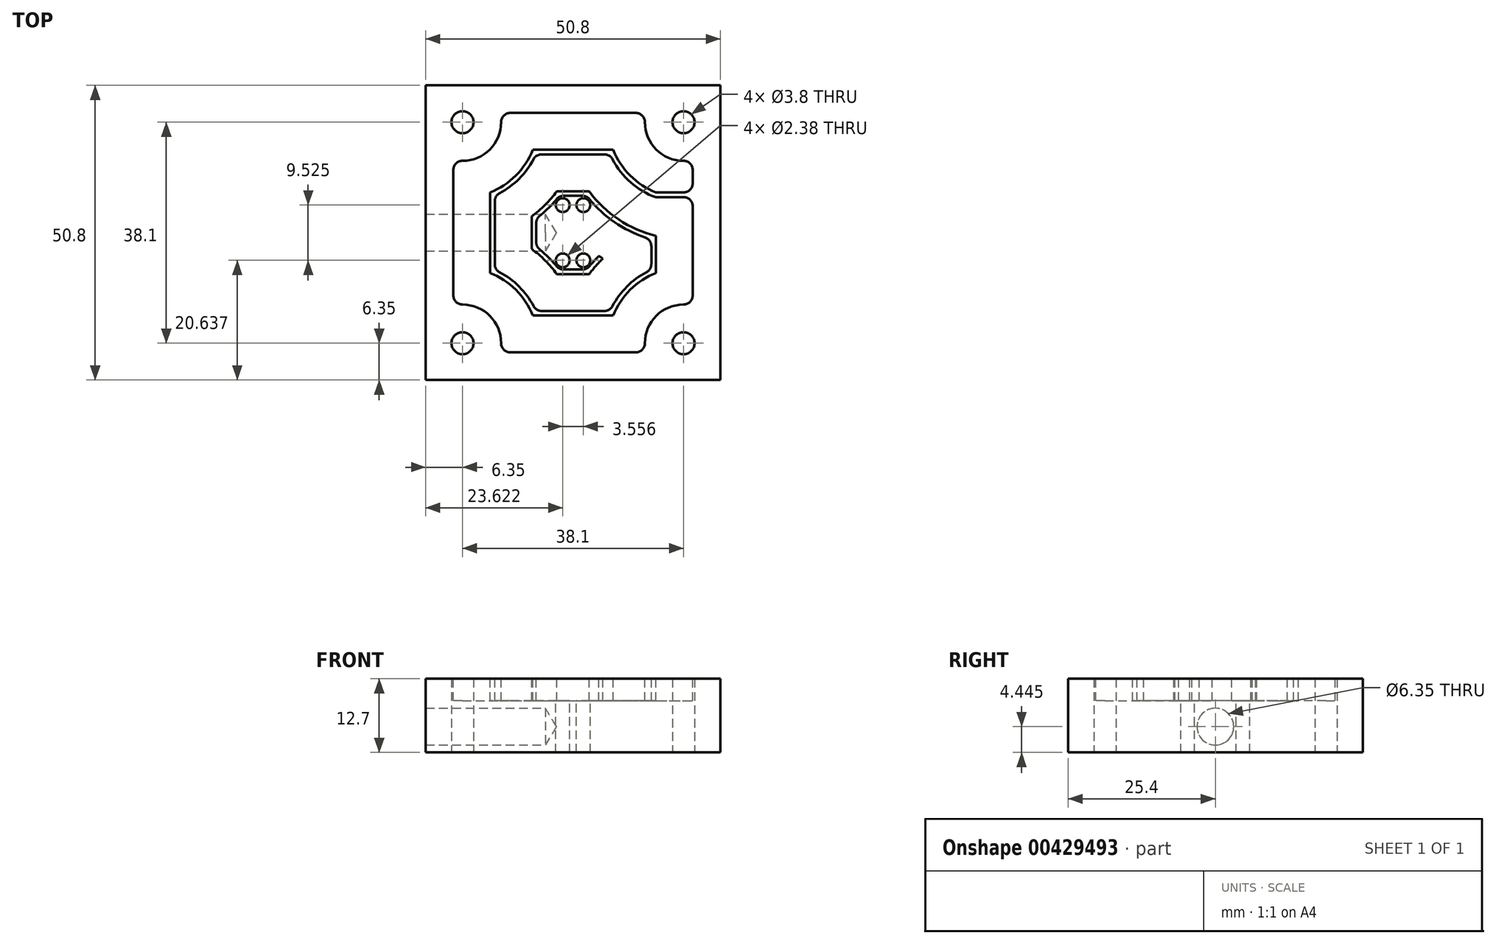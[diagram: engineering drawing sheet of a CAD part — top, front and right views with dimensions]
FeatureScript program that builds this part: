
annotation { "Feature Type Name" : "Feature", "Feature Type Description" : "" }
export const myFeature = defineFeature(function(context is Context, id is Id, definition is map)
    precondition{}
    {
        {
            var Q0;
            Q0=qCreatedBy(makeId("Top.planeOp"),FACE);
            var sketch = newSketch(context, id + "F0", { "sketchPlane" : qUnion([Q0])});
            skLineSegment(sketch, "E0.bottom", {"start": v(-25.4, 25.4) * mm, "end": v(25.4, 25.4) * mm});
            skLineSegment(sketch, "E0.top", {"start": v(-25.4, -25.4) * mm, "end": v(25.4, -25.4) * mm});
            skLineSegment(sketch, "E0.left", {"start": v(-25.4, 25.4) * mm, "end": v(-25.4, -25.4) * mm});
            skLineSegment(sketch, "E0.right", {"start": v(25.4, 25.4) * mm, "end": v(25.4, -25.4) * mm});
            skSolve(sketch);
        }
        {
            var Q0;
            Q0=makeQuery(id+"F0.imprint","IMPRINT",FACE,{"disambiguationData":[TD([[makeQuery(id+"F0.imprint","IMPRINT",EDGE,{"derivedFrom":sQuery(id+"F0.wireOp",EDGE,"E0.bottom")}),-1.0]])]});
            extrude(context, id + "F1", {"entities" : qUnion([Q0]), "depth" : 12.7 * mm, "offsetDistance" : 25.4 * mm});
        }
        {
            var Q0;
            Q0=makeQuery(id+"F1.opExtrude","CAP_FACE",FACE,{"disambiguationData":[OSD([sQuery(id+"F0.wireOp",EDGE,"E0.bottom"),sQuery(id+"F0.wireOp",EDGE,"E0.top"),sQuery(id+"F0.wireOp",EDGE,"E0.left"),sQuery(id+"F0.wireOp",EDGE,"E0.right")])],"isStart":false});
            var sketch = newSketch(context, id + "F2", { "sketchPlane" : qUnion([Q0])});
            skPoint(sketch, "E1", {"position": v(19.05, 19.05) * mm});
            skLineSegment(sketch, "E2", {"start": v(12.7, 25.4) * mm, "end": v(12.7, -22.23) * mm, "construction": true});
            skPoint(sketch, "E3.MirrorP", {"position": v(19.05, -19.05) * mm});
            skPoint(sketch, "E4.MirrorP", {"position": v(-19.05, -19.05) * mm});
            skPoint(sketch, "E5.MirrorP", {"position": v(-19.05, 19.05) * mm});
            skLineSegment(sketch, "E6.0", {"start": v(14.29, 25.4) * mm, "end": v(14.29, -3.17) * mm, "construction": true});
            skLineSegment(sketch, "E7.MirrorCS", {"start": v(11.11, 25.4) * mm, "end": v(11.11, -3.17) * mm, "construction": true});
            skCircle(sketch, "E8", {"center": v(19.05, 19.05) * mm, "radius": 1.75 * mm, "construction": true});
            skCircle(sketch, "E9.MirrorC", {"center": v(19.05, -19.05) * mm, "radius": 1.75 * mm, "construction": true});
            skCircle(sketch, "E10.MirrorC", {"center": v(-19.05, 19.05) * mm, "radius": 1.75 * mm, "construction": true});
            skCircle(sketch, "E11.MirrorC", {"center": v(-19.05, -19.05) * mm, "radius": 1.75 * mm, "construction": true});
            skLineSegment(sketch, "E12", {"start": v(-25.4, 0) * mm, "end": v(25.4, 0) * mm, "construction": true});
            skLineSegment(sketch, "E13.0", {"start": v(-25.4, -3.18) * mm, "end": v(25.4, -3.17) * mm, "construction": true});
            skLineSegment(sketch, "E14.MirrorCS", {"start": v(-25.4, 3.18) * mm, "end": v(25.4, 3.17) * mm, "construction": true});
            skCircle(sketch, "E15", {"center": v(0, 0) * mm, "radius": 22.23 * mm, "construction": true});
            skLineSegment(sketch, "E16.0", {"start": v(-22.23, -4.76) * mm, "end": v(22.23, -4.76) * mm});
            skLineSegment(sketch, "E17.0", {"start": v(-20.64, -6.35) * mm, "end": v(22.23, -6.35) * mm});
            skLineSegment(sketch, "E18.0", {"start": v(-20.76, -7.94) * mm, "end": v(22.23, -7.94) * mm});
            skLineSegment(sketch, "E19.0", {"start": v(-22.23, -9.53) * mm, "end": v(20.64, -9.52) * mm});
            skLineSegment(sketch, "E20.0", {"start": v(-22.23, -11.11) * mm, "end": v(20.64, -11.11) * mm});
            skLineSegment(sketch, "E21.0", {"start": v(-20.64, -12.7) * mm, "end": v(22.23, -12.7) * mm});
            skLineSegment(sketch, "E22.0", {"start": v(-20.64, -14.29) * mm, "end": v(13.5, -14.29) * mm});
            skLineSegment(sketch, "E23.0", {"start": v(-22.23, -15.88) * mm, "end": v(13.5, -15.88) * mm});
            skLineSegment(sketch, "E24.0", {"start": v(-25.4, -22.23) * mm, "end": v(25.4, -22.22) * mm});
            skLineSegment(sketch, "E25.0", {"start": v(-25.4, 25.4) * mm, "end": v(-25.4, -25.4) * mm, "construction": true});
            skLineSegment(sketch, "E26.trimOffspring", {"start": v(-20.64, -12.7) * mm, "end": v(-20.64, -14.29) * mm, "construction": true});
            skLineSegment(sketch, "E27.trimOffspring", {"start": v(20.64, -9.52) * mm, "end": v(20.64, -11.11) * mm});
            skLineSegment(sketch, "E28.trimOffspring", {"start": v(22.23, -7.94) * mm, "end": v(22.23, -12.7) * mm});
            skLineSegment(sketch, "E29.trimOffspring", {"start": v(-20.64, -6.35) * mm, "end": v(-20.64, -7.94) * mm, "construction": true});
            skLineSegment(sketch, "E30.trimOffspring", {"start": v(22.23, -4.76) * mm, "end": v(22.23, -6.35) * mm});
            skLineSegment(sketch, "E31.trimOffspring", {"start": v(-22.23, -4.76) * mm, "end": v(-22.23, -9.53) * mm, "construction": true});
            skLineSegment(sketch, "E32.trimOffspring", {"start": v(-22.23, -11.11) * mm, "end": v(-22.23, -15.88) * mm, "construction": true});
            skLineSegment(sketch, "E33.trimOffspring", {"start": v(11.9, -14.29) * mm, "end": v(11.9, -15.88) * mm});
            skLineSegment(sketch, "E34.trimOffspring", {"start": v(13.5, -14.29) * mm, "end": v(13.5, -15.88) * mm});
            skSolve(sketch);
        }
        {
            var Q0;
            {var subQ1=sQuery(id+"F2.wireOp",EDGE,"E24.0");Q0=makeQuery(id+"F2.imprint","IMPRINT",FACE,{"disambiguationData":[TD([[makeQuery(id+"F2.imprint","IMPRINT",EDGE,{"derivedFrom":subQ1}),1.0]])]});}
            var sketch = newSketch(context, id + "F3", { "sketchPlane" : qUnion([Q0])});
            skLineSegment(sketch, "E35.0", {"start": v(-25.4, 3.18) * mm, "end": v(25.4, 3.17) * mm, "construction": true});
            skLineSegment(sketch, "E36.0", {"start": v(-25.4, -3.18) * mm, "end": v(25.4, -3.17) * mm, "construction": true});
            skLineSegment(sketch, "E37.0", {"start": v(12.7, 25.4) * mm, "end": v(12.7, -22.23) * mm, "construction": true});
            skLineSegment(sketch, "E38.0", {"start": v(14.29, 25.4) * mm, "end": v(14.29, -3.17) * mm, "construction": true});
            skCircle(sketch, "E39.0", {"center": v(19.05, -19.05) * mm, "radius": 1.75 * mm, "construction": true});
            skCircle(sketch, "E40.0", {"center": v(19.05, 19.05) * mm, "radius": 1.75 * mm, "construction": true});
            skCircle(sketch, "E41.0", {"center": v(-19.05, 19.05) * mm, "radius": 1.75 * mm, "construction": true});
            skCircle(sketch, "E42.0", {"center": v(-19.05, -19.05) * mm, "radius": 1.75 * mm, "construction": true});
            skLineSegment(sketch, "E43.0", {"start": v(-25.4, -25.4) * mm, "end": v(25.4, -25.4) * mm, "construction": true});
            skLineSegment(sketch, "E44.0", {"start": v(25.4, 25.4) * mm, "end": v(25.4, -25.4) * mm, "construction": true});
            skLineSegment(sketch, "E45.0", {"start": v(-25.4, 25.4) * mm, "end": v(25.4, 25.4) * mm, "construction": true});
            skLineSegment(sketch, "E46.0", {"start": v(-25.4, 25.4) * mm, "end": v(-25.4, -25.4) * mm, "construction": true});
            skArc(sketch, "E47.0", {"start": v(14.29, 20.31) * mm, "mid": v(15.14, 16.05) * mm, "end": v(19.05, 14.12) * mm});
            skArc(sketch, "E48.0", {"start": v(-14.12, -19.05) * mm, "mid": v(-15.57, -15.57) * mm, "end": v(-19.05, -14.12) * mm});
            skArc(sketch, "E49.MirrorC", {"start": v(14.12, -19.05) * mm, "mid": v(15.57, -15.57) * mm, "end": v(19.05, -14.12) * mm});
            skArc(sketch, "E50.MirrorC", {"start": v(-14.12, 19.05) * mm, "mid": v(-15.57, 15.57) * mm, "end": v(-19.05, 14.12) * mm});
            skArc(sketch, "E51.trimOffspring", {"start": v(9.36, -19.05) * mm, "mid": v(11.66, -12.78) * mm, "end": v(17.46, -9.5) * mm});
            skArc(sketch, "E52.MirrorCS", {"start": v(9.5, 17.46) * mm, "mid": v(12.2, 12.2) * mm, "end": v(17.46, 9.5) * mm});
            skLineSegment(sketch, "E53", {"start": v(9.36, -19.05) * mm, "end": v(9.36, -22.23) * mm});
            skArc(sketch, "E54.MirrorCS", {"start": v(-9.5, 17.46) * mm, "mid": v(-12.2, 12.2) * mm, "end": v(-17.46, 9.5) * mm});
            skArc(sketch, "E55.MirrorCS", {"start": v(-9.5, -17.46) * mm, "mid": v(-12.2, -12.2) * mm, "end": v(-17.46, -9.5) * mm});
            skPoint(sketch, "E56.orphan", {"position": v(-9.36, -19.05) * mm});
            skLineSegment(sketch, "E57.trimOffspring", {"start": v(-9.5, 17.46) * mm, "end": v(9.5, 17.46) * mm});
            skLineSegment(sketch, "E58.trimOffspring", {"start": v(-9.5, -17.46) * mm, "end": v(3.89, -17.46) * mm});
            skLineSegment(sketch, "E59", {"start": v(19.05, -14.12) * mm, "end": v(19.84, -14.12) * mm});
            skLineSegment(sketch, "E60.MirrorCS", {"start": v(19.05, 14.12) * mm, "end": v(19.84, 14.12) * mm});
            skLineSegment(sketch, "E61.MirrorCS", {"start": v(-19.05, 14.12) * mm, "end": v(-19.84, 14.12) * mm});
            skLineSegment(sketch, "E62.MirrorCS", {"start": v(-19.05, -14.12) * mm, "end": v(-19.84, -14.12) * mm});
            skLineSegment(sketch, "E63", {"start": v(14.12, -19.05) * mm, "end": v(14.12, -34.5) * mm});
            skLineSegment(sketch, "E64.MirrorCS", {"start": v(14.12, 19.05) * mm, "end": v(14.12, 19.84) * mm});
            skLineSegment(sketch, "E65.MirrorCS", {"start": v(-14.12, 19.05) * mm, "end": v(-14.12, 19.84) * mm});
            skLineSegment(sketch, "E66.MirrorCS", {"start": v(-14.12, -19.05) * mm, "end": v(-14.12, -19.84) * mm});
            skLineSegment(sketch, "E67.trimOffspring", {"start": v(-17.46, 9.5) * mm, "end": v(-17.46, -9.5) * mm});
            skLineSegment(sketch, "E68.trimOffspring", {"start": v(17.46, 9.5) * mm, "end": v(17.46, -9.5) * mm});
            skLineSegment(sketch, "E69.trimOffspring", {"start": v(22.23, 11.74) * mm, "end": v(22.23, -11.74) * mm});
            skLineSegment(sketch, "E70.trimOffspring", {"start": v(-11.74, 22.23) * mm, "end": v(11.74, 22.23) * mm});
            skLineSegment(sketch, "E71.trimOffspring", {"start": v(-11.74, -22.23) * mm, "end": v(6.18, -22.23) * mm});
            skLineSegment(sketch, "E72.trimOffspring", {"start": v(-22.23, 11.74) * mm, "end": v(-22.23, -11.74) * mm});
            skPoint(sketch, "E73.visualSharp", {"position": v(22.23, -14.12) * mm});
            skArc(sketch, "E73.filletArc", {"start": v(19.84, -14.12) * mm, "mid": v(21.53, -13.42) * mm, "end": v(22.23, -11.74) * mm});
            skPoint(sketch, "E74.visualSharp", {"position": v(22.23, 14.12) * mm});
            skArc(sketch, "E74.filletArc", {"start": v(22.23, 11.74) * mm, "mid": v(21.53, 13.42) * mm, "end": v(19.84, 14.12) * mm});
            skPoint(sketch, "E75.visualSharp", {"position": v(14.12, 22.23) * mm});
            skArc(sketch, "E75.filletArc", {"start": v(14.12, 19.84) * mm, "mid": v(13.42, 21.53) * mm, "end": v(11.74, 22.23) * mm});
            skPoint(sketch, "E76.visualSharp", {"position": v(-14.12, 22.23) * mm});
            skArc(sketch, "E76.filletArc", {"start": v(-11.74, 22.23) * mm, "mid": v(-13.42, 21.53) * mm, "end": v(-14.12, 19.84) * mm});
            skPoint(sketch, "E77.visualSharp", {"position": v(-22.23, 14.12) * mm});
            skArc(sketch, "E77.filletArc", {"start": v(-19.84, 14.12) * mm, "mid": v(-21.53, 13.42) * mm, "end": v(-22.23, 11.74) * mm});
            skPoint(sketch, "E78.visualSharp", {"position": v(-22.23, -14.12) * mm});
            skArc(sketch, "E78.filletArc", {"start": v(-22.23, -11.74) * mm, "mid": v(-21.53, -13.42) * mm, "end": v(-19.84, -14.12) * mm});
            skPoint(sketch, "E79.visualSharp", {"position": v(-14.12, -22.23) * mm});
            skArc(sketch, "E79.filletArc", {"start": v(-14.12, -19.84) * mm, "mid": v(-13.42, -21.53) * mm, "end": v(-11.74, -22.23) * mm});
            skLineSegment(sketch, "E80.0", {"start": v(8.57, -19.05) * mm, "end": v(8.57, -19.84) * mm});
            skArc(sketch, "E81.0", {"start": v(8.57, -19.05) * mm, "mid": v(10.37, -13.17) * mm, "end": v(15.17, -9.31) * mm});
            skLineSegment(sketch, "E82.0", {"start": v(16.67, 7.1) * mm, "end": v(16.67, -7.1) * mm});
            skArc(sketch, "E83.0", {"start": v(9.31, 15.17) * mm, "mid": v(11.64, 11.64) * mm, "end": v(15.17, 9.31) * mm});
            skLineSegment(sketch, "E84.0", {"start": v(-7.1, 16.67) * mm, "end": v(7.1, 16.67) * mm});
            skArc(sketch, "E85.0", {"start": v(-9.31, 15.17) * mm, "mid": v(-11.64, 11.64) * mm, "end": v(-15.17, 9.31) * mm});
            skLineSegment(sketch, "E86.0", {"start": v(-16.67, 7.1) * mm, "end": v(-16.67, -7.1) * mm});
            skArc(sketch, "E87.0", {"start": v(-9.31, -15.17) * mm, "mid": v(-11.64, -11.64) * mm, "end": v(-15.17, -9.31) * mm});
            skLineSegment(sketch, "E88.0", {"start": v(-7.1, -16.67) * mm, "end": v(1.25, -16.67) * mm});
            skLineSegment(sketch, "E89.trimOffspring", {"start": v(9.36, -22.23) * mm, "end": v(14.12, -22.23) * mm});
            skPoint(sketch, "E90.visualSharp", {"position": v(8.57, -22.23) * mm});
            skArc(sketch, "E90.filletArc", {"start": v(6.18, -22.23) * mm, "mid": v(7.87, -21.53) * mm, "end": v(8.57, -19.84) * mm});
            skArc(sketch, "E91.0", {"start": v(3.89, -17.46) * mm, "mid": v(6.41, -10.52) * mm, "end": v(11.9, -5.58) * mm});
            skLineSegment(sketch, "E92.0", {"start": v(11.9, 5.58) * mm, "end": v(11.9, -5.58) * mm});
            skLineSegment(sketch, "E93.MirrorCS", {"start": v(-11.9, 5.58) * mm, "end": v(-11.9, -5.58) * mm});
            skLineSegment(sketch, "E94.0", {"start": v(-5.58, -11.9) * mm, "end": v(-0.49, -11.9) * mm});
            skLineSegment(sketch, "E95.0", {"start": v(-5.58, 11.9) * mm, "end": v(5.58, 11.9) * mm});
            skArc(sketch, "E96.trimOffspring", {"start": v(5.58, 11.9) * mm, "mid": v(8.27, 8.27) * mm, "end": v(11.9, 5.58) * mm});
            skArc(sketch, "E97.trimOffspring", {"start": v(-5.58, 11.9) * mm, "mid": v(-8.27, 8.27) * mm, "end": v(-11.9, 5.58) * mm});
            skArc(sketch, "E98.trimOffspring", {"start": v(-5.58, -11.9) * mm, "mid": v(-8.27, -8.27) * mm, "end": v(-11.9, -5.58) * mm});
            skPoint(sketch, "E99.visualSharp", {"position": v(16.67, -8.84) * mm});
            skArc(sketch, "E99.filletArc", {"start": v(15.17, -9.31) * mm, "mid": v(16.26, -8.44) * mm, "end": v(16.67, -7.1) * mm});
            skPoint(sketch, "E100.visualSharp", {"position": v(16.67, 8.84) * mm});
            skArc(sketch, "E100.filletArc", {"start": v(16.67, 7.1) * mm, "mid": v(16.26, 8.44) * mm, "end": v(15.17, 9.31) * mm});
            skPoint(sketch, "E101.visualSharp", {"position": v(8.84, 16.67) * mm});
            skArc(sketch, "E101.filletArc", {"start": v(9.31, 15.17) * mm, "mid": v(8.44, 16.26) * mm, "end": v(7.1, 16.67) * mm});
            skPoint(sketch, "E102.visualSharp", {"position": v(-8.84, 16.67) * mm});
            skArc(sketch, "E102.filletArc", {"start": v(-7.1, 16.67) * mm, "mid": v(-8.44, 16.26) * mm, "end": v(-9.31, 15.17) * mm});
            skPoint(sketch, "E103.visualSharp", {"position": v(-16.67, 8.84) * mm});
            skArc(sketch, "E103.filletArc", {"start": v(-15.17, 9.31) * mm, "mid": v(-16.26, 8.44) * mm, "end": v(-16.67, 7.1) * mm});
            skPoint(sketch, "E104.visualSharp", {"position": v(-16.67, -8.84) * mm});
            skArc(sketch, "E104.filletArc", {"start": v(-16.67, -7.1) * mm, "mid": v(-16.26, -8.44) * mm, "end": v(-15.17, -9.31) * mm});
            skPoint(sketch, "E105.visualSharp", {"position": v(-8.84, -16.67) * mm});
            skArc(sketch, "E105.filletArc", {"start": v(-9.31, -15.17) * mm, "mid": v(-8.44, -16.26) * mm, "end": v(-7.1, -16.67) * mm});
            skArc(sketch, "E106.0", {"start": v(3.56, -14.9) * mm, "mid": v(5.98, -9.74) * mm, "end": v(10.07, -5.76) * mm});
            skLineSegment(sketch, "E107.0", {"start": v(11.11, 3.79) * mm, "end": v(11.11, -3.79) * mm});
            skArc(sketch, "E108.0", {"start": v(5.76, 10.07) * mm, "mid": v(7.7, 7.7) * mm, "end": v(10.07, 5.76) * mm});
            skLineSegment(sketch, "E109.0", {"start": v(-3.79, 11.11) * mm, "end": v(3.79, 11.11) * mm});
            skArc(sketch, "E110.0", {"start": v(-5.76, 10.07) * mm, "mid": v(-7.7, 7.7) * mm, "end": v(-10.07, 5.76) * mm});
            skLineSegment(sketch, "E111.0", {"start": v(-11.11, 3.79) * mm, "end": v(-11.11, -3.79) * mm});
            skArc(sketch, "E112.0", {"start": v(-5.76, -10.07) * mm, "mid": v(-7.7, -7.7) * mm, "end": v(-10.07, -5.76) * mm});
            skArc(sketch, "E113.0", {"start": v(-0.49, -11.9) * mm, "mid": v(-0.34, -11.5) * mm, "end": v(-0.18, -11.11) * mm});
            skArc(sketch, "E114.0", {"start": v(2.57, 6.35) * mm, "mid": v(4.34, 4.34) * mm, "end": v(6.35, 2.57) * mm});
            skLineSegment(sketch, "E115.0", {"start": v(-2.57, 6.35) * mm, "end": v(2.57, 6.35) * mm});
            skArc(sketch, "E116.0", {"start": v(-2.57, 6.35) * mm, "mid": v(-4.34, 4.34) * mm, "end": v(-6.35, 2.57) * mm});
            skArc(sketch, "E117.0", {"start": v(-3.44, -5.3) * mm, "mid": v(-4.83, -3.87) * mm, "end": v(-6.35, -2.57) * mm});
            skArc(sketch, "E118.trimOffspring", {"start": v(-0.49, -11.9) * mm, "mid": v(2.27, -6.76) * mm, "end": v(6.35, -2.57) * mm});
            skLineSegment(sketch, "E119.trimOffspring", {"start": v(6.35, 2.57) * mm, "end": v(6.35, -2.57) * mm});
            skLineSegment(sketch, "E120.trimOffspring", {"start": v(-6.35, 2.57) * mm, "end": v(-6.35, -2.57) * mm});
            skPoint(sketch, "E121.visualSharp", {"position": v(11.11, -5.11) * mm});
            skArc(sketch, "E121.filletArc", {"start": v(10.07, -5.76) * mm, "mid": v(10.83, -4.9) * mm, "end": v(11.11, -3.79) * mm});
            skPoint(sketch, "E122.visualSharp", {"position": v(11.11, 5.11) * mm});
            skArc(sketch, "E122.filletArc", {"start": v(11.11, 3.79) * mm, "mid": v(10.83, 4.9) * mm, "end": v(10.07, 5.76) * mm});
            skPoint(sketch, "E123.visualSharp", {"position": v(5.11, 11.11) * mm});
            skArc(sketch, "E123.filletArc", {"start": v(5.76, 10.07) * mm, "mid": v(4.9, 10.83) * mm, "end": v(3.79, 11.11) * mm});
            skPoint(sketch, "E124.visualSharp", {"position": v(-5.11, 11.11) * mm});
            skArc(sketch, "E124.filletArc", {"start": v(-3.79, 11.11) * mm, "mid": v(-4.9, 10.83) * mm, "end": v(-5.76, 10.07) * mm});
            skPoint(sketch, "E125.visualSharp", {"position": v(-11.11, 5.11) * mm});
            skArc(sketch, "E125.filletArc", {"start": v(-10.07, 5.76) * mm, "mid": v(-10.83, 4.9) * mm, "end": v(-11.11, 3.79) * mm});
            skPoint(sketch, "E126.visualSharp", {"position": v(-11.11, -5.11) * mm});
            skArc(sketch, "E126.filletArc", {"start": v(-11.11, -3.79) * mm, "mid": v(-10.83, -4.9) * mm, "end": v(-10.07, -5.76) * mm});
            skArc(sketch, "E127.filletArc", {"start": v(-5.76, -10.07) * mm, "mid": v(-4.9, -10.83) * mm, "end": v(-3.79, -11.11) * mm});
            skPoint(sketch, "E128.visualSharp", {"position": v(3.19, -16.67) * mm});
            skArc(sketch, "E128.filletArc", {"start": v(1.25, -16.67) * mm, "mid": v(2.7, -16.18) * mm, "end": v(3.56, -14.9) * mm});
            skLineSegment(sketch, "E129.trimOffspring", {"start": v(-3.79, -11.11) * mm, "end": v(-2.6, -11.11) * mm});
            skArc(sketch, "E130.0", {"start": v(-0.44, -9.76) * mm, "mid": v(0.06, -8.76) * mm, "end": v(0.62, -7.8) * mm});
            skPoint(sketch, "E131.visualSharp", {"position": v(-1.03, -11.11) * mm});
            skArc(sketch, "E131.filletArc", {"start": v(-2.6, -11.11) * mm, "mid": v(-1.32, -10.75) * mm, "end": v(-0.44, -9.76) * mm});
            skPoint(sketch, "E132", {"position": v(0, -6.35) * mm});
            skArc(sketch, "E133", {"start": v(0.62, -7.8) * mm, "mid": v(-0.17, -4.53) * mm, "end": v(-3.44, -5.3) * mm});
            skLineSegment(sketch, "E134.extension", {"start": v(-3.44, -5.3) * mm, "end": v(-3.44, -5.3) * mm});
            skSolve(sketch);
        }
        {
            var Q0;
            Q0=makeQuery(id+"F1.opExtrude","SWEPT_FACE",FACE,{"disambiguationData":[OSD([sQuery(id+"F0.wireOp",EDGE,"E0.left")])]});
            var sketch = newSketch(context, id + "F4", { "sketchPlane" : qUnion([Q0])});
            skLineSegment(sketch, "E135.0", {"start": v(-25.4, 0) * mm, "end": v(25.4, 0) * mm, "construction": true});
            skLineSegment(sketch, "E136.0", {"start": v(-25.4, 4.45) * mm, "end": v(25.4, 4.45) * mm, "construction": true});
            skPoint(sketch, "E137", {"position": v(0, 4.45) * mm});
            skLineSegment(sketch, "E138.0", {"start": v(-25.4, 12.7) * mm, "end": v(-25.4, 0) * mm, "construction": true});
            skLineSegment(sketch, "E139.0", {"start": v(25.4, 12.7) * mm, "end": v(25.4, 0) * mm, "construction": true});
            skSolve(sketch);
        }
        {
            var Q0;
            Q0=sQuery(id+"F4.wireOp",VERTEX,"E137");
            var Q1;
            Q1=makeQuery(id+"F1.opExtrude","SWEPT_BODY",BODY,{"disambiguationData":[OSD([sQuery(id+"F0.wireOp",EDGE,"E0.bottom"),sQuery(id+"F0.wireOp",EDGE,"E0.top"),sQuery(id+"F0.wireOp",EDGE,"E0.left"),sQuery(id+"F0.wireOp",EDGE,"E0.right")])]});
            hole(context, id + "F5", {"style" : HoleStyle.SIMPLE, "endStyle" : HoleEndStyle.BLIND, "holeDiameter" : 6.35 * mm, "majorDiameter" : 6.35 * mm, "holeDepth" : 20.64 * mm, "isTappedThrough" : true, "tappedDepth" : 4.44 * mm, "tapClearance" : 3, "locations" : qUnion([Q0]), "scope" : qUnion([Q1]), "startStyle" : HoleStartStyle.PART});
        }
        {
            var Q0;
            Q0=makeQuery(id+"F1.opExtrude","CAP_FACE",FACE,{"disambiguationData":[OSD([sQuery(id+"F0.wireOp",EDGE,"E0.bottom"),sQuery(id+"F0.wireOp",EDGE,"E0.top"),sQuery(id+"F0.wireOp",EDGE,"E0.left"),sQuery(id+"F0.wireOp",EDGE,"E0.right")])],"isStart":false});
            var sketch = newSketch(context, id + "F6", { "sketchPlane" : qUnion([Q0])});
            skPoint(sketch, "E140.0", {"position": v(-19.05, 19.05) * mm});
            skPoint(sketch, "E141.0", {"position": v(19.05, 19.05) * mm});
            skPoint(sketch, "E142.0", {"position": v(19.05, -19.05) * mm});
            skPoint(sketch, "E143.0", {"position": v(-19.05, -19.05) * mm});
            skSolve(sketch);
        }
        {
            var Q0;
            Q0=sQuery(id+"F6.wireOp",VERTEX,"E140.0");
            var Q1;
            Q1=sQuery(id+"F6.wireOp",VERTEX,"E141.0");
            var Q2;
            Q2=sQuery(id+"F6.wireOp",VERTEX,"E142.0");
            var Q3;
            Q3=sQuery(id+"F6.wireOp",VERTEX,"E143.0");
            var Q4;
            Q4=makeQuery(id+"F1.opExtrude","SWEPT_BODY",BODY,{"disambiguationData":[OSD([sQuery(id+"F0.wireOp",EDGE,"E0.bottom"),sQuery(id+"F0.wireOp",EDGE,"E0.top"),sQuery(id+"F0.wireOp",EDGE,"E0.left"),sQuery(id+"F0.wireOp",EDGE,"E0.right")])]});
            hole(context, id + "F7", {"style" : HoleStyle.SIMPLE, "endStyle" : HoleEndStyle.THROUGH, "standardTappedOrClearance" : lookupTablePath({ "fit" : "Free", "standard" : "ANSI", "size" : "#6", "type" : "Clearance" }), "standardBlindInLast" : lookupTablePath({ "fit" : "Free", "standard" : "ANSI", "engagement" : "75%", "pitch" : "32 tpi", "size" : "#6", "type" : "Clearance & tapped" }), "holeDiameter" : 3.8 * mm, "majorDiameter" : 6.35 * mm, "isTappedThrough" : true, "tappedDepth" : 4.44 * mm, "tapClearance" : 3, "locations" : qUnion([Q0, Q1, Q2, Q3]), "scope" : qUnion([Q4]), "startStyle" : HoleStartStyle.PART});
        }
        {
            var Q0;
            Q0=makeQuery(id+"F1.opExtrude","CAP_FACE",FACE,{"disambiguationData":[OSD([sQuery(id+"F0.wireOp",EDGE,"E0.bottom"),sQuery(id+"F0.wireOp",EDGE,"E0.top"),sQuery(id+"F0.wireOp",EDGE,"E0.left"),sQuery(id+"F0.wireOp",EDGE,"E0.right")])],"isStart":false});
            var sketch = newSketch(context, id + "F8", { "sketchPlane" : qUnion([Q0])});
            skLineSegment(sketch, "E144.0", {"start": v(-25.4, 25.4) * mm, "end": v(25.4, 25.4) * mm, "construction": true});
            skLineSegment(sketch, "E145.0", {"start": v(25.4, 25.4) * mm, "end": v(25.4, -25.4) * mm, "construction": true});
            skLineSegment(sketch, "E146.0", {"start": v(-25.4, 25.4) * mm, "end": v(-25.4, -25.4) * mm, "construction": true});
            skCircle(sketch, "E147.0", {"center": v(-19.05, -19.05) * mm, "radius": 1.9 * mm, "construction": true});
            skCircle(sketch, "E148.0", {"center": v(19.05, -19.05) * mm, "radius": 1.9 * mm, "construction": true});
            skCircle(sketch, "E149.0", {"center": v(19.05, 19.05) * mm, "radius": 1.9 * mm, "construction": true});
            skLineSegment(sketch, "E150.0", {"start": v(-25.4, 17.46) * mm, "end": v(25.4, 17.46) * mm, "construction": true});
            skLineSegment(sketch, "E151.0", {"start": v(20.64, 25.4) * mm, "end": v(20.64, 17.46) * mm});
            skLineSegment(sketch, "E152.0", {"start": v(-20.64, 25.4) * mm, "end": v(-20.64, 17.46) * mm});
            skLineSegment(sketch, "E153.0", {"start": v(-25.4, 20.64) * mm, "end": v(-20.64, 20.64) * mm});
            skLineSegment(sketch, "E154.0", {"start": v(-25.4, -20.64) * mm, "end": v(-18, -20.64) * mm});
            skArc(sketch, "E155.0", {"start": v(25.4, 17.04) * mm, "mid": v(23.76, 23.76) * mm, "end": v(17.04, 25.4) * mm});
            skArc(sketch, "E156.0", {"start": v(-17.04, 25.4) * mm, "mid": v(-23.76, 23.76) * mm, "end": v(-25.4, 17.04) * mm});
            skArc(sketch, "E157.0", {"start": v(-25.4, -17.04) * mm, "mid": v(-23.76, -23.76) * mm, "end": v(-17.04, -25.4) * mm});
            skArc(sketch, "E158.0", {"start": v(17.04, -25.4) * mm, "mid": v(23.76, -23.76) * mm, "end": v(25.4, -17.04) * mm});
            skLineSegment(sketch, "E159", {"start": v(19.05, 12.39) * mm, "end": v(19.05, 12.39) * mm});
            skLineSegment(sketch, "E160", {"start": v(19.05, -12.39) * mm, "end": v(19.05, -12.39) * mm});
            skLineSegment(sketch, "E161", {"start": v(12.39, -19.05) * mm, "end": v(12.39, -19.05) * mm});
            skLineSegment(sketch, "E162", {"start": v(-12.39, -19.05) * mm, "end": v(-12.39, -19.05) * mm});
            skLineSegment(sketch, "E163", {"start": v(-12.39, -30.54) * mm, "end": v(-12.72, -30.22) * mm});
            skLineSegment(sketch, "E164", {"start": v(-19.05, -12.39) * mm, "end": v(-19.05, -12.39) * mm});
            skLineSegment(sketch, "E165", {"start": v(-19.05, 12.39) * mm, "end": v(-19.05, 12.39) * mm});
            skLineSegment(sketch, "E166", {"start": v(-12.39, 19.05) * mm, "end": v(-12.39, 19.05) * mm});
            skLineSegment(sketch, "E167", {"start": v(12.39, 19.05) * mm, "end": v(12.39, 19.05) * mm});
            skLineSegment(sketch, "E168.trimOffspring", {"start": v(18, 20.64) * mm, "end": v(25.4, 20.64) * mm});
            skLineSegment(sketch, "E169.trimOffspring", {"start": v(12.39, 25.4) * mm, "end": v(12.39, 30.47) * mm});
            skLineSegment(sketch, "E170.trimOffspring", {"start": v(20.64, 10.8) * mm, "end": v(20.64, 8.53) * mm});
            skLineSegment(sketch, "E171.trimOffspring", {"start": v(25.4, 12.39) * mm, "end": v(31, 12.39) * mm});
            skLineSegment(sketch, "E172.trimOffspring", {"start": v(-10.8, 20.64) * mm, "end": v(10.8, 20.64) * mm});
            skLineSegment(sketch, "E173.trimOffspring", {"start": v(-12.39, 25.4) * mm, "end": v(-12.39, 29.56) * mm});
            skLineSegment(sketch, "E174.trimOffspring", {"start": v(-20.64, 10.8) * mm, "end": v(-20.64, -10.8) * mm});
            skLineSegment(sketch, "E175.trimOffspring", {"start": v(-25.4, 12.39) * mm, "end": v(-31.16, 12.39) * mm});
            skLineSegment(sketch, "E176.trimOffspring", {"start": v(-10.8, -20.64) * mm, "end": v(10.8, -20.64) * mm});
            skLineSegment(sketch, "E177.trimOffspring", {"start": v(-12.39, -25.4) * mm, "end": v(-12.39, -30.54) * mm});
            skLineSegment(sketch, "E178.trimOffspring", {"start": v(-25.4, -12.39) * mm, "end": v(-32.53, -12.39) * mm});
            skLineSegment(sketch, "E179.trimOffspring", {"start": v(-20.64, -18) * mm, "end": v(-20.64, -25.4) * mm});
            skLineSegment(sketch, "E180.trimOffspring", {"start": v(20.64, -18) * mm, "end": v(20.64, -25.4) * mm});
            skLineSegment(sketch, "E181.trimOffspring", {"start": v(25.4, -12.39) * mm, "end": v(32.2, -12.39) * mm});
            skLineSegment(sketch, "E182.trimOffspring", {"start": v(12.39, -25.4) * mm, "end": v(12.39, -30.54) * mm});
            skLineSegment(sketch, "E183.trimOffspring", {"start": v(18, -20.64) * mm, "end": v(25.4, -20.64) * mm});
            skArc(sketch, "E184.trimOffspring", {"start": v(12.39, 19.05) * mm, "mid": v(14.34, 14.34) * mm, "end": v(19.05, 12.39) * mm});
            skArc(sketch, "E185.trimOffspring", {"start": v(-19.05, 12.39) * mm, "mid": v(-14.34, 14.34) * mm, "end": v(-12.39, 19.05) * mm});
            skArc(sketch, "E186.trimOffspring", {"start": v(-12.39, -19.05) * mm, "mid": v(-14.34, -14.34) * mm, "end": v(-19.05, -12.39) * mm});
            skArc(sketch, "E187.trimOffspring", {"start": v(19.05, -12.39) * mm, "mid": v(14.34, -14.34) * mm, "end": v(12.39, -19.05) * mm});
            skLineSegment(sketch, "E188.0", {"start": v(14.29, 6.15) * mm, "end": v(14.29, 6.1) * mm});
            skArc(sketch, "E189.0", {"start": v(6.04, 19.05) * mm, "mid": v(6.06, 18.25) * mm, "end": v(6.14, 17.46) * mm});
            skLineSegment(sketch, "E190.0", {"start": v(-6.94, 14.29) * mm, "end": v(6.94, 14.29) * mm});
            skArc(sketch, "E191.0", {"start": v(-14.29, 6.94) * mm, "mid": v(-9.85, 9.85) * mm, "end": v(-6.94, 14.29) * mm});
            skLineSegment(sketch, "E192.0", {"start": v(-14.29, 6.94) * mm, "end": v(-14.29, -6.94) * mm});
            skArc(sketch, "E193.0", {"start": v(-6.94, -14.29) * mm, "mid": v(-9.85, -9.85) * mm, "end": v(-14.29, -6.94) * mm});
            skLineSegment(sketch, "E194.0", {"start": v(-6.94, -14.29) * mm, "end": v(6.94, -14.29) * mm});
            skArc(sketch, "E195.0", {"start": v(14.29, -6.94) * mm, "mid": v(9.85, -9.85) * mm, "end": v(6.94, -14.29) * mm});
            skArc(sketch, "E196.trimOffspring", {"start": v(-6.14, 17.46) * mm, "mid": v(-6.06, 18.25) * mm, "end": v(-6.04, 19.05) * mm});
            skArc(sketch, "E197.trimOffspring", {"start": v(6.94, 14.29) * mm, "mid": v(9.85, 9.85) * mm, "end": v(14.29, 6.94) * mm});
            skLineSegment(sketch, "E198", {"start": v(14.29, 6.94) * mm, "end": v(19.05, 6.94) * mm});
            skLineSegment(sketch, "E199.0", {"start": v(14.29, 6.15) * mm, "end": v(19.05, 6.15) * mm});
            skLineSegment(sketch, "E200.trimOffspring", {"start": v(25.4, 6.94) * mm, "end": v(33.62, 6.94) * mm});
            skLineSegment(sketch, "E201.trimOffspring", {"start": v(25.4, 6.15) * mm, "end": v(33.62, 6.15) * mm});
            skArc(sketch, "E202.0", {"start": v(6.82, 12.64) * mm, "mid": v(9.95, 8.67) * mm, "end": v(14.29, 6.1) * mm});
            skLineSegment(sketch, "E203.0", {"start": v(-5.42, 13.5) * mm, "end": v(5.42, 13.5) * mm});
            skArc(sketch, "E204.0", {"start": v(-12.64, 6.82) * mm, "mid": v(-9.29, 9.29) * mm, "end": v(-6.82, 12.64) * mm});
            skLineSegment(sketch, "E205.0", {"start": v(-13.5, 5.42) * mm, "end": v(-13.5, -5.42) * mm});
            skArc(sketch, "E206.0", {"start": v(-6.82, -12.64) * mm, "mid": v(-9.29, -9.29) * mm, "end": v(-12.64, -6.82) * mm});
            skLineSegment(sketch, "E207.0", {"start": v(-5.42, -13.5) * mm, "end": v(5.42, -13.5) * mm});
            skArc(sketch, "E208.0", {"start": v(12.64, -6.82) * mm, "mid": v(9.29, -9.29) * mm, "end": v(6.82, -12.64) * mm});
            skLineSegment(sketch, "E209.0", {"start": v(13.5, -2.32) * mm, "end": v(13.5, -5.42) * mm});
            skArc(sketch, "E210.0", {"start": v(2.79, 7.14) * mm, "mid": v(7.86, 2.29) * mm, "end": v(14.29, -0.53) * mm});
            skLineSegment(sketch, "E211.0", {"start": v(-2.79, 7.14) * mm, "end": v(2.79, 7.14) * mm});
            skArc(sketch, "E212.0", {"start": v(-7.14, 2.79) * mm, "mid": v(-4.8, 4.8) * mm, "end": v(-2.79, 7.14) * mm});
            skLineSegment(sketch, "E213.0", {"start": v(-7.14, 2.79) * mm, "end": v(-7.14, -2.79) * mm});
            skArc(sketch, "E214.0", {"start": v(-2.79, -7.14) * mm, "mid": v(-4.8, -4.8) * mm, "end": v(-7.14, -2.79) * mm});
            skLineSegment(sketch, "E215.0", {"start": v(-2.79, -7.14) * mm, "end": v(2.79, -7.14) * mm});
            skArc(sketch, "E216.0", {"start": v(5.16, -4.45) * mm, "mid": v(3.91, -5.74) * mm, "end": v(2.79, -7.14) * mm});
            skArc(sketch, "E217.0", {"start": v(2.85, 5.77) * mm, "mid": v(7.16, 1.8) * mm, "end": v(12.4, -0.82) * mm});
            skLineSegment(sketch, "E218.0", {"start": v(-1.62, 6.35) * mm, "end": v(1.62, 6.35) * mm});
            skArc(sketch, "E219.0", {"start": v(-5.77, 2.85) * mm, "mid": v(-4.24, 4.24) * mm, "end": v(-2.85, 5.77) * mm});
            skLineSegment(sketch, "E220.0", {"start": v(-6.35, 1.62) * mm, "end": v(-6.35, -1.62) * mm});
            skArc(sketch, "E221.0", {"start": v(-2.85, -5.77) * mm, "mid": v(-4.24, -4.24) * mm, "end": v(-5.77, -2.85) * mm});
            skLineSegment(sketch, "E222.0", {"start": v(-1.62, -6.35) * mm, "end": v(1.62, -6.35) * mm});
            skArc(sketch, "E223.0", {"start": v(4.46, -4.02) * mm, "mid": v(3.63, -4.87) * mm, "end": v(2.85, -5.77) * mm});
            skLineSegment(sketch, "E224.trimOffspring", {"start": v(14.29, -0.53) * mm, "end": v(14.29, -6.94) * mm});
            skArc(sketch, "E225.0", {"start": v(4.46, -4.02) * mm, "mid": v(4.8, -4.24) * mm, "end": v(5.16, -4.45) * mm});
            skLineSegment(sketch, "E226", {"start": v(-33.19, 0) * mm, "end": v(35.25, 0) * mm, "construction": true});
            skLineSegment(sketch, "E227.0", {"start": v(-33.19, -3.18) * mm, "end": v(35.25, -3.18) * mm, "construction": true});
            skLineSegment(sketch, "E228.MirrorCS", {"start": v(-33.19, 3.18) * mm, "end": v(35.25, 3.18) * mm, "construction": true});
            skLineSegment(sketch, "E229.0", {"start": v(-33.19, 4.76) * mm, "end": v(35.25, 4.76) * mm, "construction": true});
            skPoint(sketch, "E230", {"position": v(-1.78, 4.76) * mm});
            skCircle(sketch, "E231", {"center": v(-1.78, 4.76) * mm, "radius": 1.2 * mm});
            skCircle(sketch, "E232.MirrorC", {"center": v(1.78, 4.76) * mm, "radius": 1.2 * mm});
            skCircle(sketch, "E233.MirrorC", {"center": v(-1.78, -4.76) * mm, "radius": 1.2 * mm});
            skCircle(sketch, "E234.MirrorC", {"center": v(1.78, -4.76) * mm, "radius": 1.2 * mm});
            skPoint(sketch, "E235.visualSharp", {"position": v(12.39, 20.64) * mm});
            skArc(sketch, "E235.filletArc", {"start": v(12.39, 19.05) * mm, "mid": v(11.92, 20.17) * mm, "end": v(10.8, 20.64) * mm});
            skPoint(sketch, "E236.visualSharp", {"position": v(-12.39, 20.64) * mm});
            skArc(sketch, "E236.filletArc", {"start": v(-10.8, 20.64) * mm, "mid": v(-11.92, 20.17) * mm, "end": v(-12.39, 19.05) * mm});
            skPoint(sketch, "E237.visualSharp", {"position": v(-20.64, 12.39) * mm});
            skArc(sketch, "E237.filletArc", {"start": v(-19.05, 12.39) * mm, "mid": v(-20.17, 11.92) * mm, "end": v(-20.64, 10.8) * mm});
            skPoint(sketch, "E238.visualSharp", {"position": v(-20.64, -12.39) * mm});
            skArc(sketch, "E238.filletArc", {"start": v(-20.64, -10.8) * mm, "mid": v(-20.17, -11.92) * mm, "end": v(-19.05, -12.39) * mm});
            skPoint(sketch, "E239.visualSharp", {"position": v(-12.39, -20.64) * mm});
            skArc(sketch, "E239.filletArc", {"start": v(-12.39, -19.05) * mm, "mid": v(-11.92, -20.17) * mm, "end": v(-10.8, -20.64) * mm});
            skPoint(sketch, "E240.visualSharp", {"position": v(12.39, -20.64) * mm});
            skArc(sketch, "E240.filletArc", {"start": v(10.8, -20.64) * mm, "mid": v(11.92, -20.17) * mm, "end": v(12.39, -19.05) * mm});
            skPoint(sketch, "E241.visualSharp", {"position": v(20.64, -12.39) * mm});
            skArc(sketch, "E241.filletArc", {"start": v(19.05, -12.39) * mm, "mid": v(20.17, -11.92) * mm, "end": v(20.64, -10.8) * mm});
            skLineSegment(sketch, "E242.trimOffspring", {"start": v(20.64, 4.56) * mm, "end": v(20.64, -10.8) * mm});
            skPoint(sketch, "E243.visualSharp", {"position": v(20.64, 6.15) * mm});
            skArc(sketch, "E243.filletArc", {"start": v(20.64, 4.56) * mm, "mid": v(20.17, 5.68) * mm, "end": v(19.05, 6.15) * mm});
            skPoint(sketch, "E244.visualSharp", {"position": v(6.41, 13.5) * mm});
            skArc(sketch, "E244.filletArc", {"start": v(6.82, 12.64) * mm, "mid": v(6.24, 13.26) * mm, "end": v(5.42, 13.5) * mm});
            skPoint(sketch, "E245.visualSharp", {"position": v(-6.41, 13.5) * mm});
            skArc(sketch, "E245.filletArc", {"start": v(-5.42, 13.5) * mm, "mid": v(-6.24, 13.26) * mm, "end": v(-6.82, 12.64) * mm});
            skPoint(sketch, "E246.visualSharp", {"position": v(-13.5, 6.41) * mm});
            skArc(sketch, "E246.filletArc", {"start": v(-12.64, 6.82) * mm, "mid": v(-13.26, 6.24) * mm, "end": v(-13.5, 5.42) * mm});
            skPoint(sketch, "E247.visualSharp", {"position": v(-13.5, -6.41) * mm});
            skArc(sketch, "E247.filletArc", {"start": v(-13.5, -5.42) * mm, "mid": v(-13.26, -6.24) * mm, "end": v(-12.64, -6.82) * mm});
            skPoint(sketch, "E248.visualSharp", {"position": v(-6.41, -13.5) * mm});
            skArc(sketch, "E248.filletArc", {"start": v(-6.82, -12.64) * mm, "mid": v(-6.24, -13.26) * mm, "end": v(-5.42, -13.5) * mm});
            skPoint(sketch, "E249.visualSharp", {"position": v(6.41, -13.5) * mm});
            skArc(sketch, "E249.filletArc", {"start": v(5.42, -13.5) * mm, "mid": v(6.24, -13.26) * mm, "end": v(6.82, -12.64) * mm});
            skPoint(sketch, "E250.visualSharp", {"position": v(13.5, -6.41) * mm});
            skArc(sketch, "E250.filletArc", {"start": v(12.64, -6.82) * mm, "mid": v(13.26, -6.24) * mm, "end": v(13.5, -5.42) * mm});
            skPoint(sketch, "E251.visualSharp", {"position": v(13.5, -1.15) * mm});
            skArc(sketch, "E251.filletArc", {"start": v(13.5, -2.32) * mm, "mid": v(13.2, -1.4) * mm, "end": v(12.4, -0.82) * mm});
            skPoint(sketch, "E252.visualSharp", {"position": v(2.39, 6.35) * mm});
            skArc(sketch, "E252.filletArc", {"start": v(2.85, 5.77) * mm, "mid": v(2.3, 6.2) * mm, "end": v(1.62, 6.35) * mm});
            skPoint(sketch, "E253.visualSharp", {"position": v(-2.39, 6.35) * mm});
            skArc(sketch, "E253.filletArc", {"start": v(-1.62, 6.35) * mm, "mid": v(-2.3, 6.2) * mm, "end": v(-2.85, 5.77) * mm});
            skPoint(sketch, "E254.visualSharp", {"position": v(-6.35, 2.39) * mm});
            skArc(sketch, "E254.filletArc", {"start": v(-5.77, 2.85) * mm, "mid": v(-6.2, 2.3) * mm, "end": v(-6.35, 1.62) * mm});
            skPoint(sketch, "E255.visualSharp", {"position": v(-6.35, -2.39) * mm});
            skArc(sketch, "E255.filletArc", {"start": v(-6.35, -1.62) * mm, "mid": v(-6.2, -2.3) * mm, "end": v(-5.77, -2.85) * mm});
            skPoint(sketch, "E256.visualSharp", {"position": v(-2.39, -6.35) * mm});
            skArc(sketch, "E256.filletArc", {"start": v(-2.85, -5.77) * mm, "mid": v(-2.3, -6.2) * mm, "end": v(-1.62, -6.35) * mm});
            skPoint(sketch, "E257.visualSharp", {"position": v(2.39, -6.35) * mm});
            skArc(sketch, "E257.filletArc", {"start": v(1.62, -6.35) * mm, "mid": v(2.3, -6.2) * mm, "end": v(2.85, -5.77) * mm});
            skPoint(sketch, "E258.visualSharp", {"position": v(20.64, 6.94) * mm});
            skArc(sketch, "E258.filletArc", {"start": v(19.05, 6.94) * mm, "mid": v(20.17, 7.4) * mm, "end": v(20.64, 8.53) * mm});
            skPoint(sketch, "E259.visualSharp", {"position": v(20.64, 12.39) * mm});
            skArc(sketch, "E259.filletArc", {"start": v(20.64, 10.8) * mm, "mid": v(20.17, 11.92) * mm, "end": v(19.05, 12.39) * mm});
            skPoint(sketch, "E260.0", {"position": v(25.4, -25.4) * mm});
            skPoint(sketch, "E261.0", {"position": v(-25.4, -25.4) * mm});
            skLineSegment(sketch, "E262.0", {"start": v(-25.4, -25.4) * mm, "end": v(25.4, -25.4) * mm, "construction": true});
            skSolve(sketch);
        }
        {
            var Q0;
            Q0=makeQuery(id+"F8.imprint","IMPRINT",FACE,{"disambiguationData":[TD([[makeQuery(id+"F8.imprint","IMPRINT",EDGE,{"derivedFrom":sQuery(id+"F8.wireOp",EDGE,"E170.trimOffspring")}),-1.0]])]});
            var Q1;
            Q1=makeQuery(id+"F8.imprint","IMPRINT",FACE,{"disambiguationData":[TD([[makeQuery(id+"F8.imprint","IMPRINT",EDGE,{"derivedFrom":sQuery(id+"F8.wireOp",EDGE,"E231")}),1.0]])]});
            var Q2;
            Q2=makeQuery(id+"F8.imprint","IMPRINT",FACE,{"disambiguationData":[TD([[makeQuery(id+"F8.imprint","IMPRINT",EDGE,{"derivedFrom":sQuery(id+"F8.wireOp",EDGE,"E232.MirrorC")}),-1.0]])]});
            var Q3;
            Q3=makeQuery(id+"F8.imprint","IMPRINT",FACE,{"disambiguationData":[TD([[makeQuery(id+"F8.imprint","IMPRINT",EDGE,{"derivedFrom":sQuery(id+"F8.wireOp",EDGE,"E234.MirrorC")}),1.0]])]});
            var Q4;
            Q4=makeQuery(id+"F8.imprint","IMPRINT",FACE,{"disambiguationData":[TD([[makeQuery(id+"F8.imprint","IMPRINT",EDGE,{"derivedFrom":sQuery(id+"F8.wireOp",EDGE,"E233.MirrorC")}),-1.0]])]});
            extrude(context, id + "F9", {"entities" : qUnion([Q0, Q1, Q2, Q3, Q4]), "operationType" : NewBodyOperationType.REMOVE, "oppositeDirection" : true, "depth" : 3.8 * mm, "offsetDistance" : 25.4 * mm});
        }
        {
            var Q0;
            Q0=makeQuery(id+"F8.imprint","IMPRINT",FACE,{"disambiguationData":[TD([[makeQuery(id+"F8.imprint","IMPRINT",EDGE,{"derivedFrom":sQuery(id+"F8.wireOp",EDGE,"E170.trimOffspring")}),-1.0]])]});
            var sketch = newSketch(context, id + "F10", { "sketchPlane" : qUnion([Q0])});
            skCircle(sketch, "E263.0", {"center": v(-1.78, 4.76) * mm, "radius": 1.2 * mm});
            skCircle(sketch, "E264.0", {"center": v(1.78, 4.76) * mm, "radius": 1.2 * mm});
            skCircle(sketch, "E265.0", {"center": v(1.78, -4.76) * mm, "radius": 1.2 * mm});
            skCircle(sketch, "E266.0", {"center": v(-1.78, -4.76) * mm, "radius": 1.2 * mm});
            skSolve(sketch);
        }
        {
            var Q0;
            Q0 = qSketchRegion(id + "F10", true);
            extrude(context, id + "F11", {"entities" : qUnion([Q0]), "operationType" : NewBodyOperationType.REMOVE, "endBound" : BoundingType.THROUGH_ALL, "oppositeDirection" : true, "depth" : 25.4 * mm, "offsetDistance" : 25.4 * mm});
        }
    });
